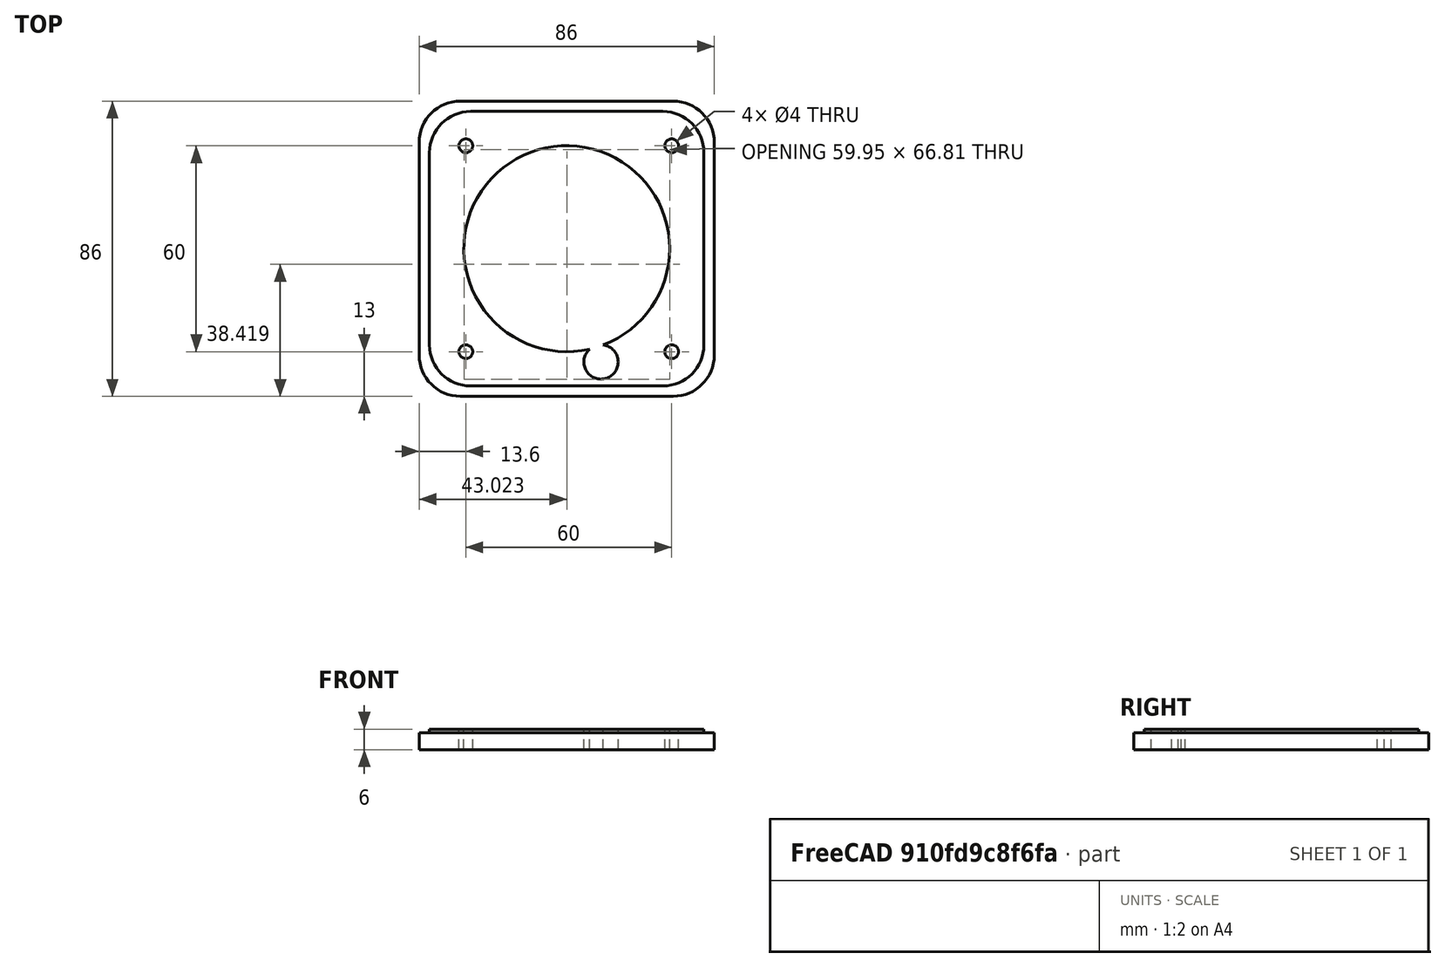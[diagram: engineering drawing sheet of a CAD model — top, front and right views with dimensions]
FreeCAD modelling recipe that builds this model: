
FCSTD DOCUMENT  (FreeCAD 0.17R13522 (Git))
Label: frontspeaker
License: All rights reserved
LicenseURL: http://en.wikipedia.org/wiki/All_rights_reserved
objects: Part::Cylinder×6, Part::Box×2, Part::Fillet×2, Part::MultiFuse×2, Part::Cut×1
note: 13 computed .brp shape members not serialized (recipe doc carries the construction recipe); baked Part::Feature solids carry a one-line shape summary decoded from their .brp

FEATURE [Part::Box] Box003  label="Cubo003"
  AttacherType = Attacher::AttachEngine3D
  Height = 1
  Length = 80
  Width = 80
FEATURE [Part::Fillet] Fillet002
  Base = -> Box003
  Edges = 4 edges r=12: [Edge1,Edge3,Edge5,Edge7]
FEATURE [Part::Box] Box004  label="Cubo004"
  AttacherType = Attacher::AttachEngine3D
  Height = 5
  Length = 86
  Width = 86
FEATURE [Part::Fillet] Fillet003
  Base = -> Box004
  Edges = 4 edges r=12: [Edge1,Edge3,Edge5,Edge7]
  Placement = pos=(-3,-3,-5) rot=(0,0,1;0rad)
FEATURE [Part::Cylinder] Cylinder008  label="Speaker"
  Angle = 360
  AttacherType = Attacher::AttachEngine3D
  Height = 10
  Placement = pos=(42,42,-6) rot=(0,0,1;0rad)
  Radius = 30
FEATURE [Part::Cylinder] Cylinder009  label="LED"
  Angle = 360
  AttacherType = Attacher::AttachEngine3D
  Height = 10
  Placement = pos=(52,9,-6) rot=(0,0,1;0rad)
  Radius = 5
FEATURE [Part::MultiFuse] Fusion001  label="Tapa"
  Placement = pos=(2,2,0) rot=(0,0,1;0rad)
  Shapes = -> [Fillet002,Fillet003]
FEATURE [Part::Cylinder] Cylinder011  label="rod1"
  Angle = 360
  AttacherType = Attacher::AttachEngine3D
  Height = 63
  Placement = pos=(72.6,12,-9) rot=(0,0,1;0rad)
  Radius = 2
FEATURE [Part::Cylinder] Cylinder012  label="rod2"
  Angle = 360
  AttacherType = Attacher::AttachEngine3D
  Height = 63
  Placement = pos=(72.6,72,-9) rot=(0,0,1;0rad)
  Radius = 2
FEATURE [Part::Cylinder] Cylinder013  label="rod3"
  Angle = 360
  AttacherType = Attacher::AttachEngine3D
  Height = 63
  Placement = pos=(12.6,12,-9) rot=(0,0,1;0rad)
  Radius = 2
FEATURE [Part::Cylinder] Cylinder014  label="rod4"
  Angle = 360
  AttacherType = Attacher::AttachEngine3D
  Height = 63
  Placement = pos=(12.6,72,-9) rot=(0,0,1;0rad)
  Radius = 2
FEATURE [Part::MultiFuse] Fusion003  label="holes"
  Shapes = -> [Cylinder011,Cylinder009,Cylinder008,Cylinder012,Cylinder013,Cylinder014]
FEATURE [Part::Cut] Cut005  label="frontspeaker"
  Base = -> Fusion001
  Tool = -> Fusion003
